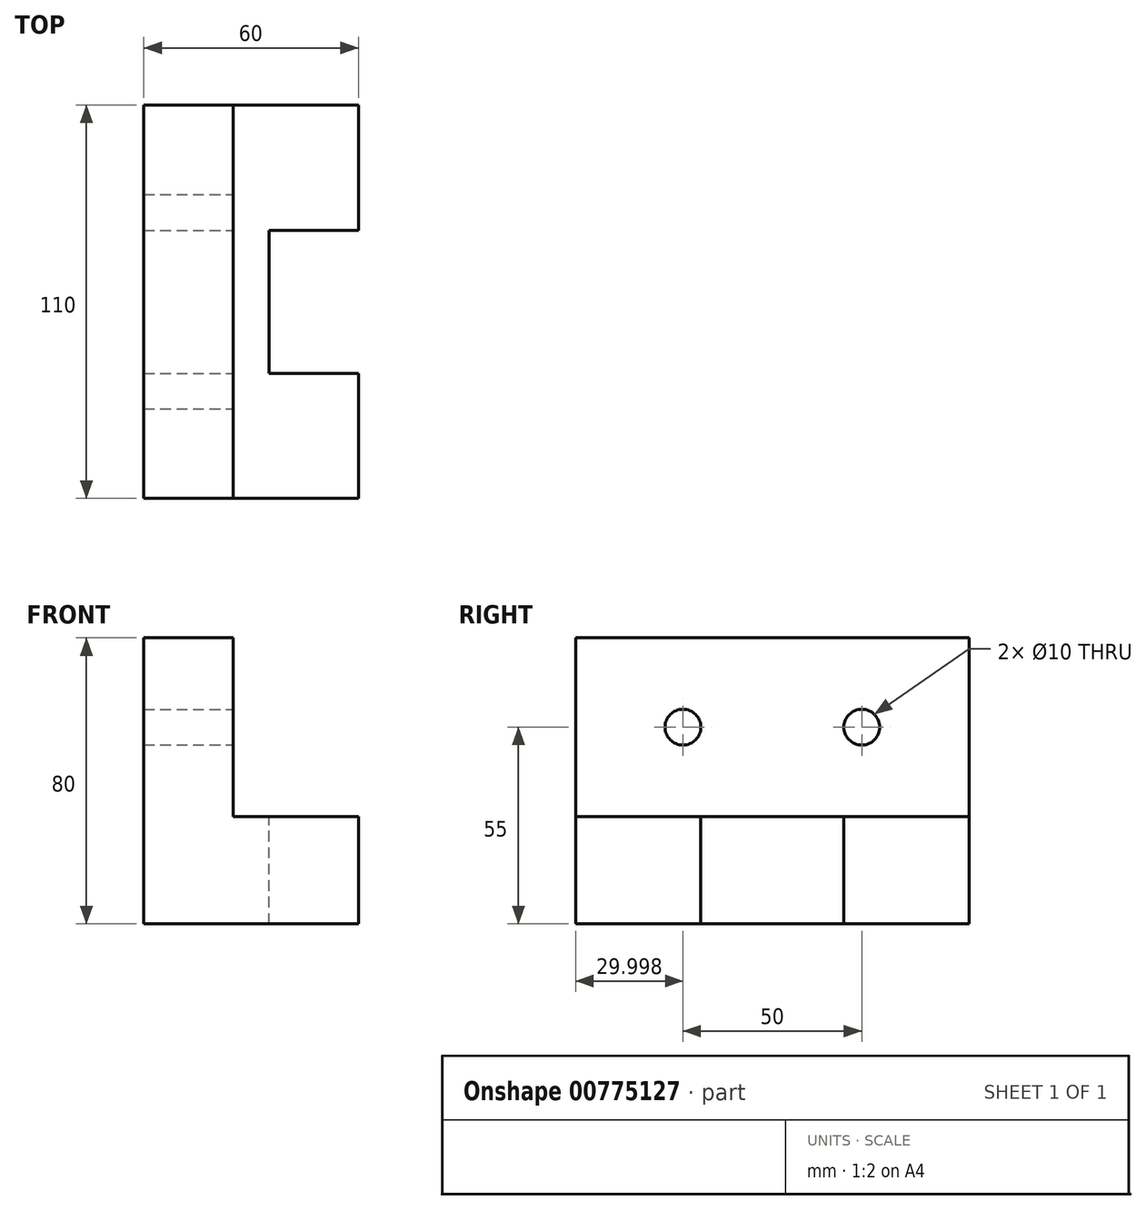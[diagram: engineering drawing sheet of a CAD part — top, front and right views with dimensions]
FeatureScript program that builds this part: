
annotation { "Feature Type Name" : "Feature", "Feature Type Description" : "" }
export const myFeature = defineFeature(function(context is Context, id is Id, definition is map)
    precondition{}
    {
        {
            var Q0;
            Q0=qCreatedBy(makeId("Top.planeOp"),FACE);
            var sketch = newSketch(context, id + "F0", { "sketchPlane" : qUnion([Q0])});
            skLineSegment(sketch, "E0.bottom", {"start": v(-58.96, 93.09) * mm, "end": v(1.04, 93.09) * mm});
            skLineSegment(sketch, "E0.top", {"start": v(-58.96, -16.91) * mm, "end": v(1.04, -16.91) * mm});
            skLineSegment(sketch, "E0.left", {"start": v(-58.96, 93.09) * mm, "end": v(-58.96, -16.91) * mm});
            skLineSegment(sketch, "E0.right", {"start": v(1.04, 93.09) * mm, "end": v(1.04, -16.91) * mm});
            skSolve(sketch);
        }
        {
            var Q0;
            Q0=makeQuery(id+"F0.imprint","IMPRINT",FACE,{"disambiguationData":[TD([[makeQuery(id+"F0.imprint","IMPRINT",EDGE,{"derivedFrom":sQuery(id+"F0.wireOp",EDGE,"E0.bottom")}),-1.0]])]});
            extrude(context, id + "F1", {"entities" : qUnion([Q0]), "depth" : 80 * mm, "offsetDistance" : 25 * mm});
        }
        {
            var Q0;
            Q0=makeQuery(id+"F1.opExtrude","SWEPT_FACE",FACE,{"disambiguationData":[OSD([sQuery(id+"F0.wireOp",EDGE,"E0.top")])]});
            var sketch = newSketch(context, id + "F2", { "sketchPlane" : qUnion([Q0])});
            skPoint(sketch, "E1", {"position": v(1.04, 30) * mm});
            skPoint(sketch, "E2", {"position": v(-33.96, 80) * mm});
            skPoint(sketch, "E3", {"position": v(-33.96, 30) * mm});
            skLineSegment(sketch, "E4.bottom", {"start": v(-33.96, 30) * mm, "end": v(1.04, 30) * mm});
            skLineSegment(sketch, "E4.top", {"start": v(-33.96, 80) * mm, "end": v(1.04, 80) * mm});
            skLineSegment(sketch, "E4.left", {"start": v(-33.96, 30) * mm, "end": v(-33.96, 80) * mm});
            skLineSegment(sketch, "E4.right", {"start": v(1.04, 30) * mm, "end": v(1.04, 80) * mm});
            skSolve(sketch);
        }
        {
            var Q0;
            Q0=makeQuery(id+"F2.imprint","IMPRINT",FACE,{"disambiguationData":[TD([[makeQuery(id+"F2.imprint","IMPRINT",EDGE,{"derivedFrom":sQuery(id+"F2.wireOp",EDGE,"E4.bottom")}),1.0]])]});
            extrude(context, id + "F3", {"entities" : qUnion([Q0]), "operationType" : NewBodyOperationType.REMOVE, "oppositeDirection" : true, "depth" : 110 * mm, "offsetDistance" : 25 * mm});
        }
        {
            var Q0;
            Q0=makeQuery(id+"F3.boolean.opBoolean","COPY",FACE,{"derivedFrom":makeQuery(id+"F3.opExtrude","SWEPT_FACE",FACE,{"disambiguationData":[OSD([sQuery(id+"F2.wireOp",EDGE,"E4.bottom")])]})});
            var sketch = newSketch(context, id + "F4", { "sketchPlane" : qUnion([Q0])});
            skPoint(sketch, "E5", {"position": v(-23.96, 58.09) * mm});
            skPoint(sketch, "E6", {"position": v(-23.96, 18.09) * mm});
            skLineSegment(sketch, "E7.bottom", {"start": v(-23.96, 58.09) * mm, "end": v(1.04, 58.09) * mm});
            skLineSegment(sketch, "E7.top", {"start": v(-23.96, 18.09) * mm, "end": v(1.04, 18.09) * mm});
            skLineSegment(sketch, "E7.left", {"start": v(-23.96, 58.09) * mm, "end": v(-23.96, 18.09) * mm});
            skLineSegment(sketch, "E7.right", {"start": v(1.04, 58.09) * mm, "end": v(1.04, 18.09) * mm});
            skSolve(sketch);
        }
        {
            var Q0;
            Q0=makeQuery(id+"F4.imprint","IMPRINT",FACE,{"disambiguationData":[TD([[makeQuery(id+"F4.imprint","IMPRINT",EDGE,{"derivedFrom":sQuery(id+"F4.wireOp",EDGE,"E7.bottom")}),-1.0]])]});
            extrude(context, id + "F5", {"entities" : qUnion([Q0]), "operationType" : NewBodyOperationType.REMOVE, "oppositeDirection" : true, "depth" : 30 * mm, "offsetDistance" : 25 * mm});
        }
        {
            var Q0;
            Q0=makeQuery(id+"F3.boolean.opBoolean","COPY",FACE,{"derivedFrom":makeQuery(id+"F3.opExtrude","SWEPT_FACE",FACE,{"disambiguationData":[OSD([sQuery(id+"F2.wireOp",EDGE,"E4.left")])]})});
            var sketch = newSketch(context, id + "F6", { "sketchPlane" : qUnion([Q0])});
            skPoint(sketch, "E8", {"position": v(-16.91, 55) * mm});
            skPoint(sketch, "E9", {"position": v(13.09, 55) * mm});
            skPoint(sketch, "E10", {"position": v(63.09, 55) * mm});
            skCircle(sketch, "E11", {"center": v(13.09, 55) * mm, "radius": 5 * mm});
            skCircle(sketch, "E12", {"center": v(63.09, 55) * mm, "radius": 5 * mm});
            skSolve(sketch);
        }
        {
            var Q0;
            Q0=makeQuery(id+"F6.imprint","IMPRINT",FACE,{"disambiguationData":[TD([[makeQuery(id+"F6.imprint","IMPRINT",EDGE,{"derivedFrom":sQuery(id+"F6.wireOp",EDGE,"E11")}),1.0]])]});
            var Q1;
            Q1=makeQuery(id+"F6.imprint","IMPRINT",FACE,{"disambiguationData":[TD([[makeQuery(id+"F6.imprint","IMPRINT",EDGE,{"derivedFrom":sQuery(id+"F6.wireOp",EDGE,"E12")}),1.0]])]});
            extrude(context, id + "F7", {"entities" : qUnion([Q0, Q1]), "operationType" : NewBodyOperationType.REMOVE, "oppositeDirection" : true, "depth" : 25 * mm, "offsetDistance" : 25 * mm});
        }
    });
